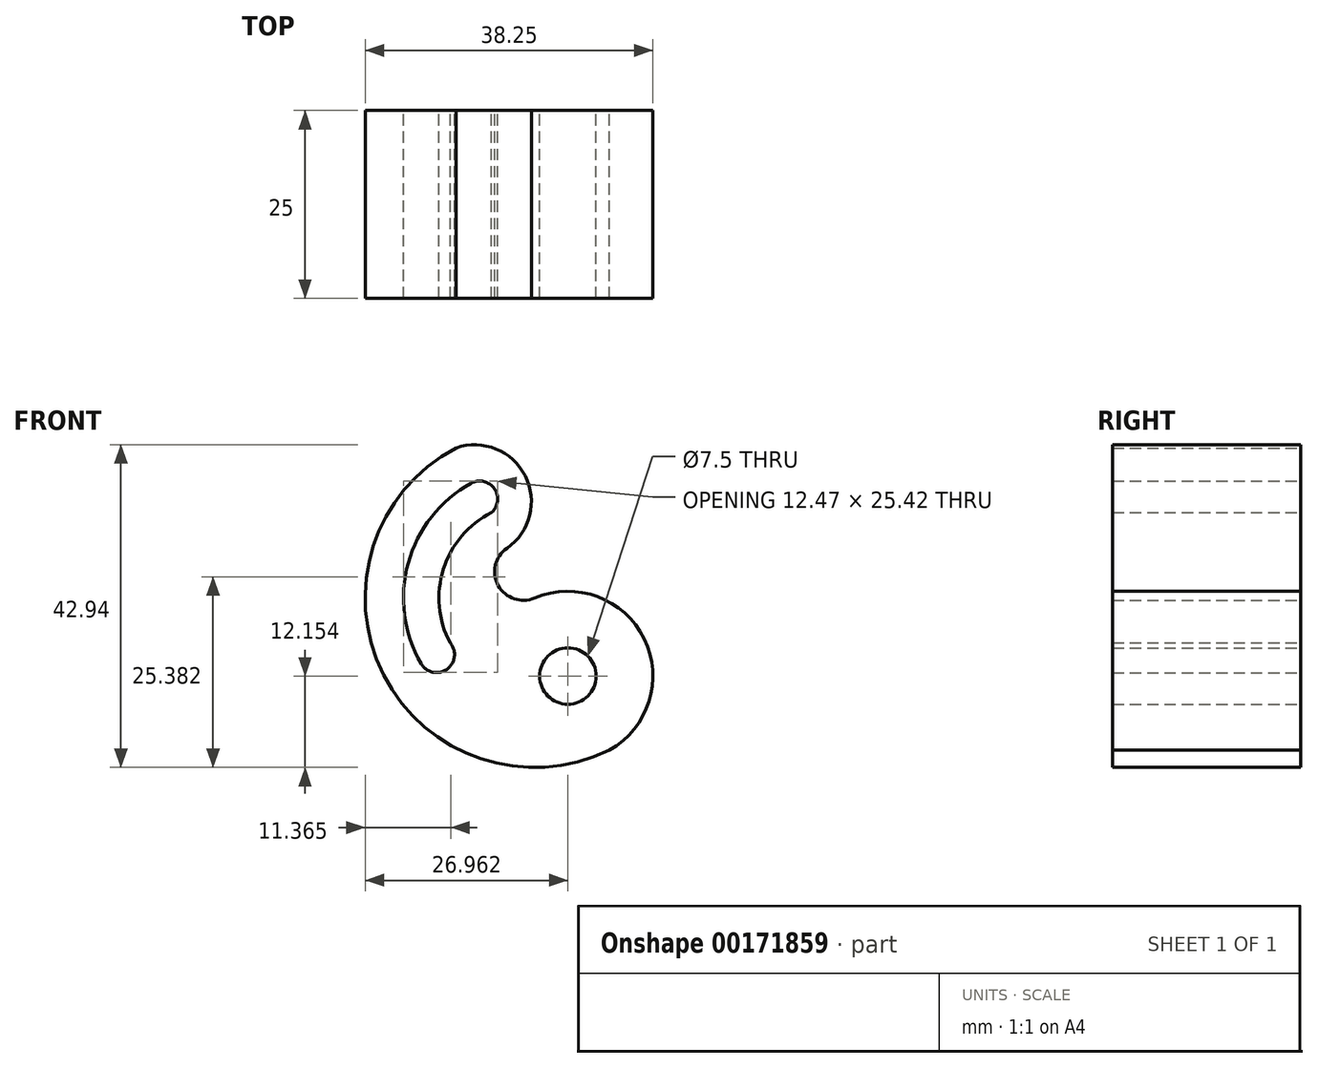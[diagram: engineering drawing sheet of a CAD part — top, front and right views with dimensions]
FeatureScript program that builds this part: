
annotation { "Feature Type Name" : "Feature", "Feature Type Description" : "" }
export const myFeature = defineFeature(function(context is Context, id is Id, definition is map)
    precondition{}
    {
        {
            var Q0;
            Q0=qCreatedBy(makeId("Front.planeOp"),FACE);
            var sketch = newSketch(context, id + "F0", { "sketchPlane" : qUnion([Q0])});
            skArc(sketch, "E0", {"start": v(-10.46, 19.98) * mm, "mid": v(-20.12, -10.2) * mm, "end": v(9.93, -20.25) * mm});
            skArc(sketch, "E1", {"start": v(-8.49, 15.26) * mm, "mid": v(-16.83, 4.66) * mm, "end": v(-15.13, -8.73) * mm});
            skArc(sketch, "E2", {"start": v(-5.76, 11.36) * mm, "mid": v(-12.15, 3.84) * mm, "end": v(-11.25, -5.98) * mm});
            skArc(sketch, "E3.trimOffspring", {"start": v(-3.69, 6.63) * mm, "mid": v(-1.26, 16.25) * mm, "end": v(-10.46, 19.98) * mm});
            skArc(sketch, "E4", {"start": v(9.93, -20.25) * mm, "mid": v(14.55, -5.42) * mm, "end": v(0, 0) * mm});
            skCircle(sketch, "E5", {"center": v(4.41, -10.4) * mm, "radius": 3.75 * mm});
            skArc(sketch, "E6", {"start": v(-3.69, 6.63) * mm, "mid": v(-4.84, 1.65) * mm, "end": v(0, 0) * mm});
            skArc(sketch, "E7", {"start": v(-15.13, -8.73) * mm, "mid": v(-11.67, -9.48) * mm, "end": v(-11.25, -5.98) * mm});
            skArc(sketch, "E8", {"start": v(-8.49, 15.26) * mm, "mid": v(-5.36, 14.54) * mm, "end": v(-5.76, 11.36) * mm});
            skSolve(sketch);
        }
        {
            var Q0;
            Q0=makeQuery(id+"F0.imprint","IMPRINT",FACE,{"disambiguationData":[TD([[makeQuery(id+"F0.imprint","IMPRINT",EDGE,{"derivedFrom":sQuery(id+"F0.wireOp",EDGE,"E0")}),1.0]])]});
            extrude(context, id + "F1", {"entities" : qUnion([Q0]), "depth" : 25 * mm});
        }
    });
